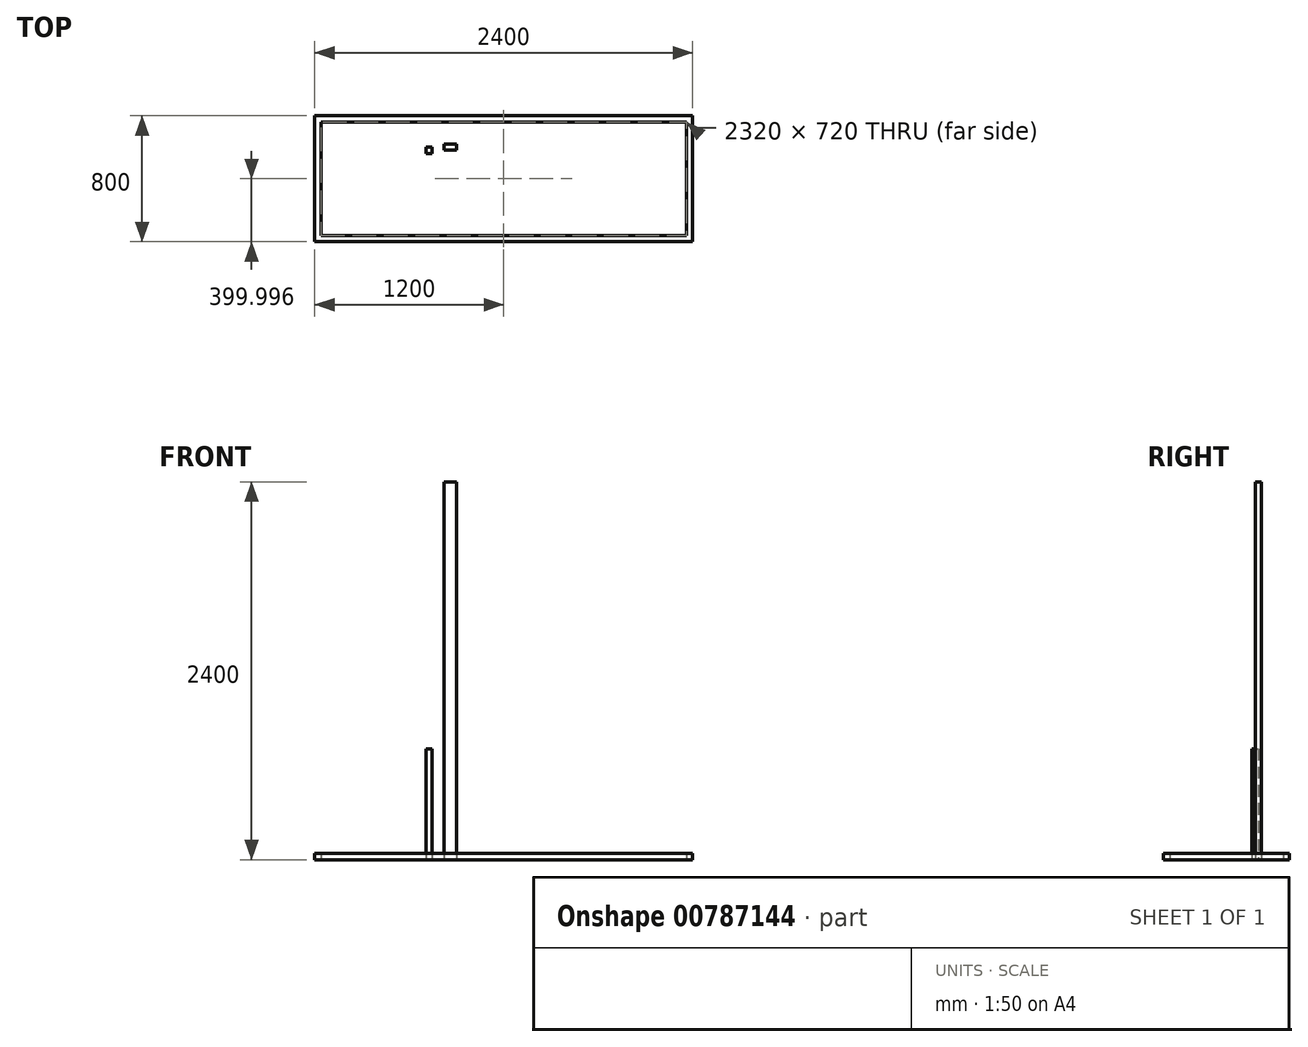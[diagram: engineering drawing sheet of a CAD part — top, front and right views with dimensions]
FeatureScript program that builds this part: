
annotation { "Feature Type Name" : "Feature", "Feature Type Description" : "" }
export const myFeature = defineFeature(function(context is Context, id is Id, definition is map)
    precondition{}
    {
        {
            var Q0;
            Q0=qCreatedBy(makeId("Top.planeOp"),FACE);
            var sketch = newSketch(context, id + "F0", { "sketchPlane" : qUnion([Q0])});
            skLineSegment(sketch, "E0.bottom", {"start": v(109.6, -621.42) * mm, "end": v(-2290.4, -621.42) * mm});
            skLineSegment(sketch, "E0.top", {"start": v(109.6, 178.58) * mm, "end": v(-2290.4, 178.58) * mm});
            skLineSegment(sketch, "E0.left", {"start": v(109.6, -621.42) * mm, "end": v(109.6, 178.58) * mm});
            skLineSegment(sketch, "E0.right", {"start": v(-2290.4, -621.42) * mm, "end": v(-2290.4, 178.58) * mm});
            skPoint(sketch, "E0.middle", {"position": v(-1090.4, -221.42) * mm});
            skLineSegment(sketch, "E1.bottom", {"start": v(69.6, -581.42) * mm, "end": v(-2250.4, -581.42) * mm});
            skLineSegment(sketch, "E1.top", {"start": v(69.6, 138.58) * mm, "end": v(-2250.4, 138.58) * mm});
            skLineSegment(sketch, "E1.left", {"start": v(69.6, -581.42) * mm, "end": v(69.6, 138.58) * mm});
            skLineSegment(sketch, "E1.right", {"start": v(-2250.4, -581.42) * mm, "end": v(-2250.4, 138.58) * mm});
            skSolve(sketch);
        }
        {
            var Q0;
            Q0=makeQuery(id+"F0.imprint","IMPRINT",FACE,{"disambiguationData":[TD([[makeQuery(id+"F0.imprint","IMPRINT",EDGE,{"derivedFrom":sQuery(id+"F0.wireOp",EDGE,"E0.bottom")}),-1.0]])]});
            extrude(context, id + "F1", {"entities" : qUnion([Q0]), "depth" : 40 * mm, "offsetDistance" : 25 * mm});
        }
        {
            var Q0;
            Q0=qCreatedBy(makeId("Top.planeOp"),FACE);
            var sketch = newSketch(context, id + "F2", { "sketchPlane" : qUnion([Q0])});
            skLineSegment(sketch, "E2.bottom", {"start": v(-1544.55, -61.15) * mm, "end": v(-1584.55, -61.15) * mm});
            skLineSegment(sketch, "E2.top", {"start": v(-1544.55, -21.15) * mm, "end": v(-1584.55, -21.15) * mm});
            skLineSegment(sketch, "E2.left", {"start": v(-1544.55, -61.15) * mm, "end": v(-1544.55, -21.15) * mm});
            skLineSegment(sketch, "E2.right", {"start": v(-1584.55, -61.15) * mm, "end": v(-1584.55, -21.15) * mm});
            skPoint(sketch, "E2.middle", {"position": v(-1564.55, -41.15) * mm});
            skSolve(sketch);
        }
        {
            var Q0;
            Q0 = qSketchRegion(id + "F2", true);
            extrude(context, id + "F3", {"entities" : qUnion([Q0]), "depth" : 705 * mm, "offsetDistance" : 25 * mm});
        }
        {
            var Q0;
            Q0=qCreatedBy(makeId("Top.planeOp"),FACE);
            var sketch = newSketch(context, id + "F4", { "sketchPlane" : qUnion([Q0])});
            skLineSegment(sketch, "E3.bottom", {"start": v(-1387.82, -39.83) * mm, "end": v(-1467.82, -39.83) * mm});
            skLineSegment(sketch, "E3.top", {"start": v(-1387.82, 0.17) * mm, "end": v(-1467.82, 0.17) * mm});
            skLineSegment(sketch, "E3.left", {"start": v(-1387.82, -39.83) * mm, "end": v(-1387.82, 0.17) * mm});
            skLineSegment(sketch, "E3.right", {"start": v(-1467.82, -39.83) * mm, "end": v(-1467.82, 0.17) * mm});
            skPoint(sketch, "E3.middle", {"position": v(-1427.82, -19.83) * mm});
            skSolve(sketch);
        }
        {
            var Q0;
            Q0 = qSketchRegion(id + "F4", true);
            extrude(context, id + "F5", {"entities" : qUnion([Q0]), "depth" : 2400 * mm, "offsetDistance" : 25 * mm});
        }
    });
